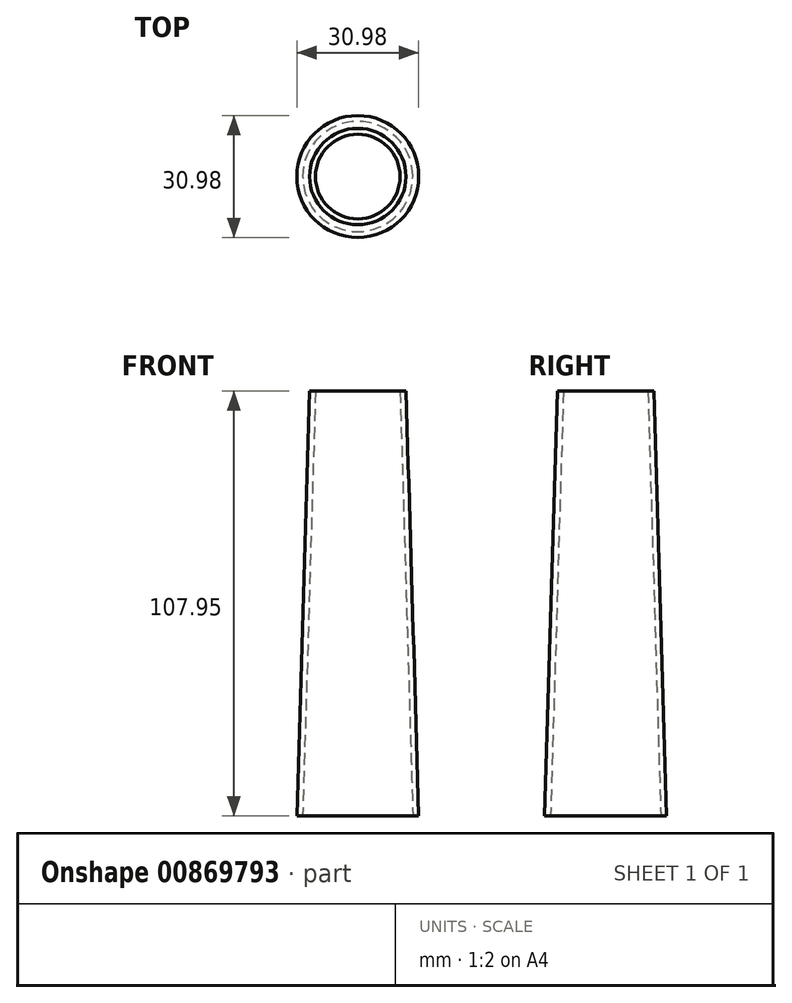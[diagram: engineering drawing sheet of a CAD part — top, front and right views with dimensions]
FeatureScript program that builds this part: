
annotation { "Feature Type Name" : "Feature", "Feature Type Description" : "" }
export const myFeature = defineFeature(function(context is Context, id is Id, definition is map)
    precondition{}
    {
        {
            var Q0;
            Q0=qCreatedBy(makeId("Front.planeOp"),FACE);
            var sketch = newSketch(context, id + "F0", { "sketchPlane" : qUnion([Q0])});
            skLineSegment(sketch, "E0", {"start": v(-10.75, 63.16) * mm, "end": v(-12.25, 63.16) * mm});
            skLineSegment(sketch, "E1", {"start": v(-12.25, 63.16) * mm, "end": v(-15.5, -44.8) * mm});
            skLineSegment(sketch, "E2", {"start": v(-15.5, -44.8) * mm, "end": v(-14, -44.8) * mm});
            skLineSegment(sketch, "E3", {"start": v(-13.99, -44.8) * mm, "end": v(-10.75, 63.16) * mm});
            skLineSegment(sketch, "E4", {"start": v(0, 14.77) * mm, "end": v(0, 9.4) * mm});
            skSolve(sketch);
        }
        {
            var Q0;
            Q0=makeQuery(id+"F0.imprint","IMPRINT",FACE,{"disambiguationData":[TD([[makeQuery(id+"F0.imprint","IMPRINT",EDGE,{"derivedFrom":sQuery(id+"F0.wireOp",EDGE,"E0")}),1.0]])]});
            var Q1;
            Q1=sQuery(id+"F0.wireOp",EDGE,"E4");
            revolve(context, id + "F1", {"surfaceOperationType" : NewSurfaceOperationType.NEW, "entities" : qUnion([Q0]), "axis" : qUnion([Q1]), "revolveType" : RevolveType.FULL});
        }
    });
